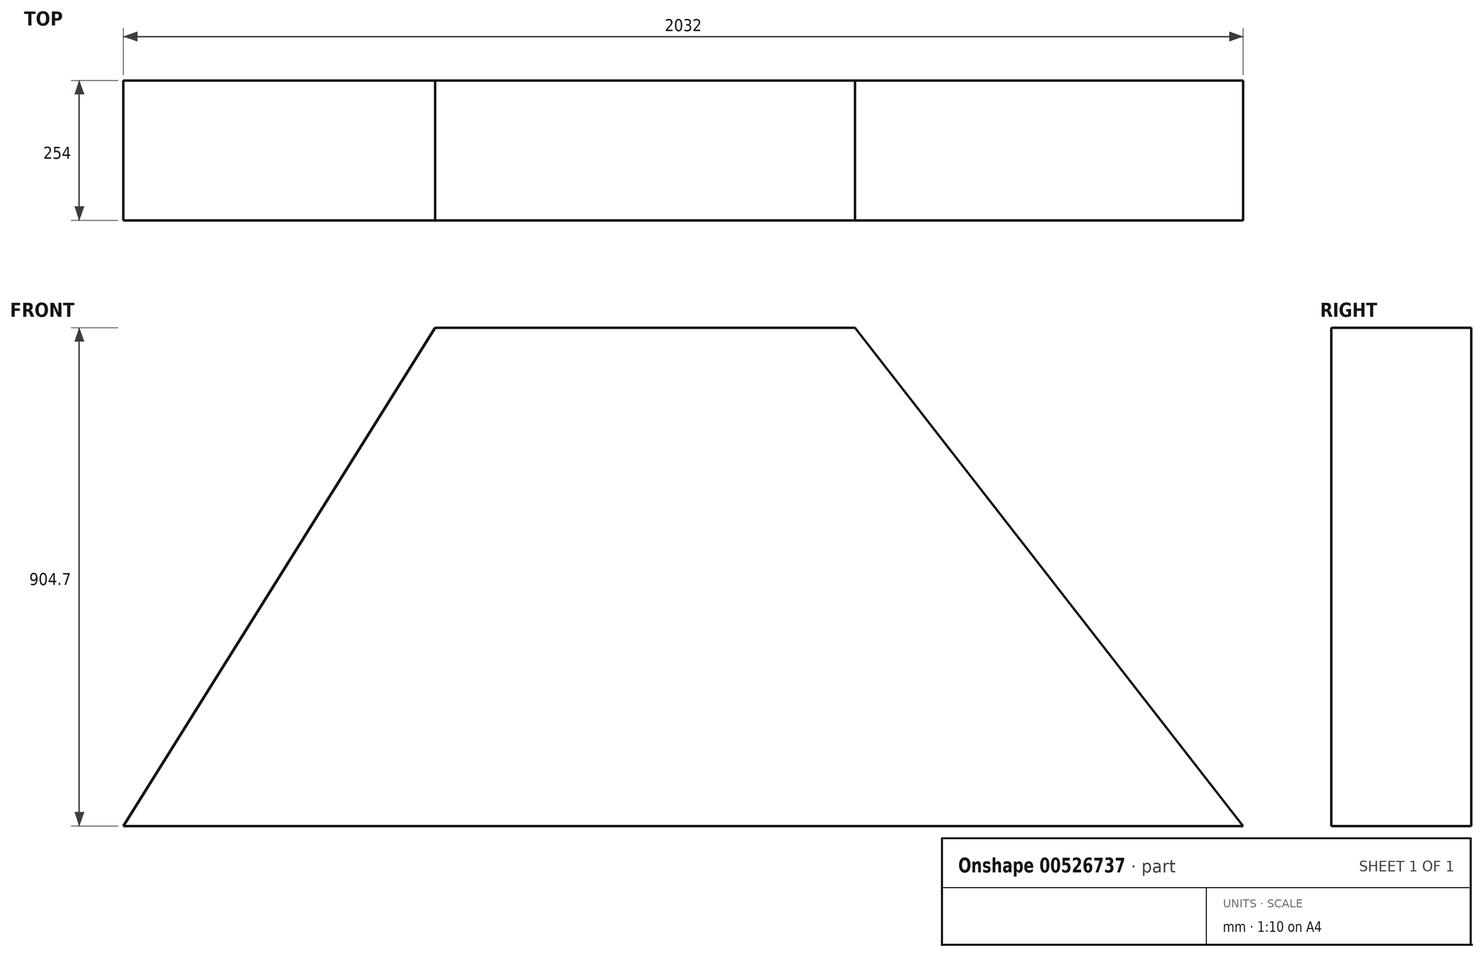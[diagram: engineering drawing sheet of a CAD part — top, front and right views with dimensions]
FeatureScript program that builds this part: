
annotation { "Feature Type Name" : "Feature", "Feature Type Description" : "" }
export const myFeature = defineFeature(function(context is Context, id is Id, definition is map)
    precondition{}
    {
        {
            var Q0;
            Q0=qCreatedBy(makeId("Front.planeOp"),FACE);
            var sketch = newSketch(context, id + "F0", { "sketchPlane" : qUnion([Q0])});
            skLineSegment(sketch, "E0", {"start": v(0, 0) * mm, "end": v(2032, 0) * mm});
            skLineSegment(sketch, "E1", {"start": v(2032, 0) * mm, "end": v(1327.32, 904.7) * mm});
            skLineSegment(sketch, "E2", {"start": v(1327.32, 904.7) * mm, "end": v(565.32, 904.7) * mm});
            skLineSegment(sketch, "E3", {"start": v(565.32, 904.7) * mm, "end": v(0, 0) * mm});
            skSolve(sketch);
        }
        {
            var Q0;
            Q0=makeQuery(id+"F0.imprint","IMPRINT",FACE,{"disambiguationData":[TD([[makeQuery(id+"F0.imprint","IMPRINT",EDGE,{"derivedFrom":sQuery(id+"F0.wireOp",EDGE,"E0")}),1.0]])]});
            extrude(context, id + "F1", {"entities" : qUnion([Q0]), "depth" : 254 * mm, "offsetDistance" : 25.4 * mm});
        }
    });
